# Revit family: ASL_Designline_Skirting_Wall_Starter_64mm Stud_2x13mm Gib_Int 1x13mm Gib Ext
name_source: partatom
category: Detail Items
revit_build: Autodesk Revit 2018 (Build: 20170223_1515(x64)
units: mm (PartAtom-declared; Revit-internal decimal feet)

## family parameters
Rotate with component = No
Section Shape = Not Defined
Shared = Yes

## types (3) — shared parameters
Manufacturer = PSL Innovative Aluminium Ltd
Technical Info = http://www.productspec.net

## per-type parameters (varying)
| type | PSL408 | Skirting_100 | Skirting_120 | Skirting_150 | Type Comments |
| Skirting 100mm | No | Yes | No | No | PSL Designline Wall Starter With 100mm Skirting for PSL408 Headsection 64mm Stud 2X13mm Gib Ext 13mm Gib Int Wall |
| Skirting 120mm | Yes | No | Yes | No | PSL Designline Wall Starter With 120mm Skirting for PSL408 Headsection 64mm Stud 2X13mm Gib Ext 13mm Gib Int Wall |
| Skirting 150mm | Yes | No | No | Yes | PSL Designline Wall Starter With 150mm Skirting for PSL408 Headsection 64mm Stud 2X13mm Gib Ext 13mm Gib Int Wall |

## geometry (parser evidence)
native form markers: Sweep x4
no freeform markers — native parametric forms only
